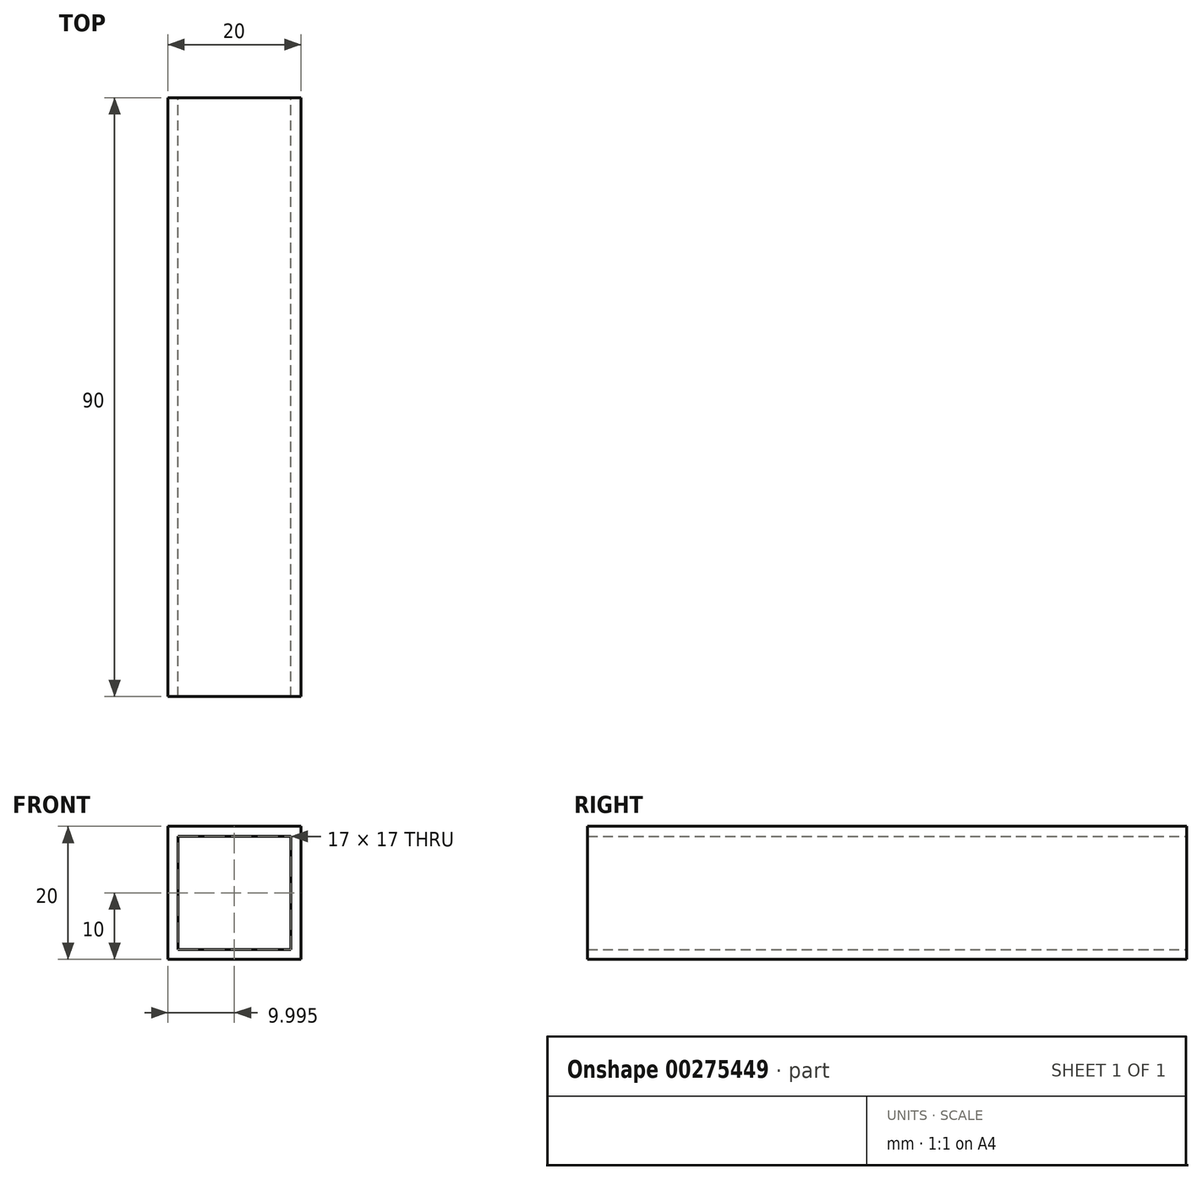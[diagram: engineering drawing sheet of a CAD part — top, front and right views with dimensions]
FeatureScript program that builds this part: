
annotation { "Feature Type Name" : "Feature", "Feature Type Description" : "" }
export const myFeature = defineFeature(function(context is Context, id is Id, definition is map)
    precondition{}
    {
        {
            var Q0;
            Q0=qCreatedBy(makeId("Front.planeOp"),FACE);
            var sketch = newSketch(context, id + "F0", { "sketchPlane" : qUnion([Q0])});
            skLineSegment(sketch, "E0.bottom", {"start": v(-34.48, 27.75) * mm, "end": v(-54.48, 27.75) * mm});
            skLineSegment(sketch, "E0.top", {"start": v(-34.48, 47.75) * mm, "end": v(-54.48, 47.75) * mm});
            skLineSegment(sketch, "E0.left", {"start": v(-34.48, 27.75) * mm, "end": v(-34.48, 47.75) * mm});
            skLineSegment(sketch, "E0.right", {"start": v(-54.48, 27.75) * mm, "end": v(-54.48, 47.75) * mm});
            skPoint(sketch, "E0.middle", {"position": v(-44.48, 37.75) * mm});
            skLineSegment(sketch, "E1.bottom", {"start": v(-35.98, 29.25) * mm, "end": v(-52.98, 29.25) * mm});
            skLineSegment(sketch, "E1.top", {"start": v(-35.98, 46.25) * mm, "end": v(-52.98, 46.25) * mm});
            skLineSegment(sketch, "E1.left", {"start": v(-35.98, 29.25) * mm, "end": v(-35.98, 46.25) * mm});
            skLineSegment(sketch, "E1.right", {"start": v(-52.98, 29.25) * mm, "end": v(-52.98, 46.25) * mm});
            skSolve(sketch);
        }
        {
            var Q0;
            Q0=makeQuery(id+"F0.imprint","IMPRINT",FACE,{"disambiguationData":[TD([[makeQuery(id+"F0.imprint","IMPRINT",EDGE,{"derivedFrom":sQuery(id+"F0.wireOp",EDGE,"E0.bottom")}),-1.0]])]});
            extrude(context, id + "F1", {"entities" : qUnion([Q0]), "depth" : 90 * mm});
        }
    });
